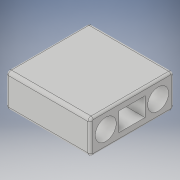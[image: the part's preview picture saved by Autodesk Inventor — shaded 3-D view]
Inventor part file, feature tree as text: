
AUTODESK INVENTOR PART (.ipt)
format: ipt  version: 2019 (Build 230136000, 136)  size: 203,776 bytes
history: native  units: mm
features: extrude x5, sketch x5, fillet x3, hole x1
ambient origin geometry x8: Origin, YZ Plane, XZ Plane, XY Plane, X Axis, Y Axis, Z Axis, Center Point
bodies: Solid1 (feature_tree)
feature tree (14):
  extrude  "Extrusion1"  Depth=80.0mm
  sketch  "Sketch27"  dims[d2=32.0mm d3=0.0mm d171=5.0mm]
  extrude  "Extrusion21"  Depth=5.0mm
  hole  "Hole8"  [1 undecoded]
  extrude  "Extrusion22"  Depth=10.0mm TaperAngle=0.0deg
  extrude  "Extrusion23"  Depth=25.0mm
  extrude  "Extrusion24"  Depth=7.0mm
  fillet  "Fillet23"  Radius=7.0mm
  fillet  "Fillet24"  Radius=25.0mm
  fillet  "Fillet25"  Radius=10.0mm
  sketch  "Sketch1"  dims[d0=80.0mm d1=80.0mm]
  sketch  "Sketch28"  dims[d172=5.0mm d173=20.0mm]
  sketch  "Sketch29"  dims[d174=20.0mm d175=10.0mm d176=0.0mm]
  sketch  "Sketch30"  dims[d177=25.0mm d178=25.0mm d179=20.0mm d180=6.0mm d181=4.0mm d182=2.0mm d183=90.0deg d184=15.0mm d185=0.0mm d186=7.0mm d187=7.0mm d188=25.0mm d189=10.0mm d190=0.0mm d191=4.0mm d192=0.0mm d193=4.0mm d194=0.0mm d195=11.0mm d196=3.0mm d197=2.0mm d12=1.0mm d13=1.0mm d14=1.0mm d15=0.15mm d16=0.25mm d17=0.375mm d18=14.3117mm d19=0.75mm d20=20.594885mm d21=0.0625mm d22=0.75mm d23=0.375mm]
note: 1 required parameter value undecoded (feature->parameter linkage not recoverable at this tier; creation-order binding heuristic only, values carry confidence <= 0.55)
